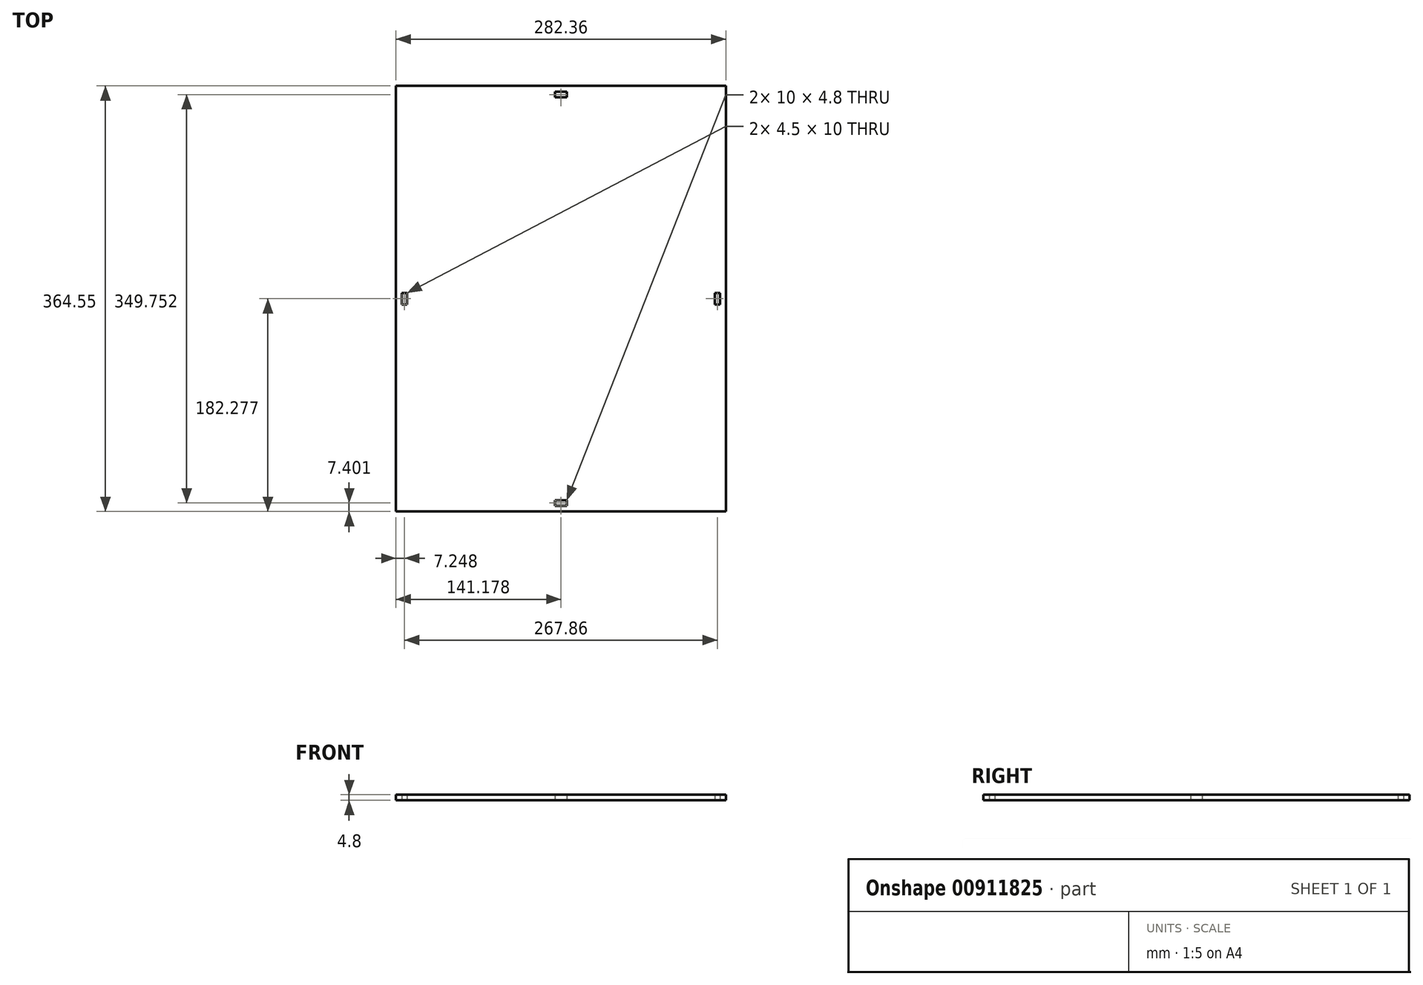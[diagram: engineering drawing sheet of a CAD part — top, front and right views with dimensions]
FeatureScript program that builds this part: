
annotation { "Feature Type Name" : "Feature", "Feature Type Description" : "" }
export const myFeature = defineFeature(function(context is Context, id is Id, definition is map)
    precondition{}
    {
        {
            var Q0;
            Q0=qCreatedBy(makeId("Top.planeOp"),FACE);
            var sketch = newSketch(context, id + "F0", { "sketchPlane" : qUnion([Q0])});
            skLineSegment(sketch, "E0.bottom", {"start": v(-131.6, 255.96) * mm, "end": v(-0.42, 255.96) * mm});
            skLineSegment(sketch, "E0.top", {"start": v(-131.6, -98.59) * mm, "end": v(-0.42, -98.59) * mm});
            skLineSegment(sketch, "E0.left", {"start": v(-131.6, 255.96) * mm, "end": v(-131.6, 83.69) * mm});
            skLineSegment(sketch, "E0.right", {"start": v(140.76, 255.96) * mm, "end": v(140.76, 83.69) * mm});
            skLineSegment(sketch, "E1", {"start": v(4.58, 251.16) * mm, "end": v(4.58, -93.79) * mm});
            skLineSegment(sketch, "E2", {"start": v(135.96, 78.69) * mm, "end": v(-126.8, 78.69) * mm});
            skLineSegment(sketch, "E3", {"start": v(136.26, 73.69) * mm, "end": v(140.76, 73.69) * mm});
            skLineSegment(sketch, "E4.MirrorCS", {"start": v(136.26, 83.69) * mm, "end": v(140.76, 83.69) * mm});
            skPoint(sketch, "E5.start.orphan", {"position": v(140.76, 78.69) * mm});
            skLineSegment(sketch, "E6.MirrorCS", {"start": v(-126.8, 73.69) * mm, "end": v(-131.6, 73.69) * mm});
            skLineSegment(sketch, "E7.MirrorCS", {"start": v(-126.8, 83.69) * mm, "end": v(-131.6, 83.69) * mm});
            skLineSegment(sketch, "E8", {"start": v(4.58, 251.16) * mm, "end": v(9.58, 251.16) * mm});
            skLineSegment(sketch, "E9", {"start": v(9.58, 251.16) * mm, "end": v(9.58, 255.96) * mm});
            skLineSegment(sketch, "E10.MirrorCS", {"start": v(4.58, 251.16) * mm, "end": v(-0.42, 251.16) * mm});
            skLineSegment(sketch, "E11.MirrorCS", {"start": v(-0.42, 251.16) * mm, "end": v(-0.42, 255.96) * mm});
            skLineSegment(sketch, "E12.MirrorCS", {"start": v(9.58, -93.79) * mm, "end": v(9.58, -98.59) * mm});
            skLineSegment(sketch, "E13.MirrorCS", {"start": v(4.58, -93.79) * mm, "end": v(9.58, -93.79) * mm});
            skLineSegment(sketch, "E14.MirrorCS", {"start": v(-0.42, -93.79) * mm, "end": v(-0.42, -98.59) * mm});
            skLineSegment(sketch, "E15.MirrorCS", {"start": v(4.58, -93.79) * mm, "end": v(-0.42, -93.79) * mm});
            skPoint(sketch, "E16.end.orphan", {"position": v(4.58, 255.96) * mm});
            skLineSegment(sketch, "E17.trimOffspring", {"start": v(9.58, 255.96) * mm, "end": v(140.76, 255.96) * mm});
            skLineSegment(sketch, "E18.trimOffspring", {"start": v(140.76, 73.69) * mm, "end": v(140.76, -98.59) * mm});
            skLineSegment(sketch, "E19.trimOffspring", {"start": v(9.58, -98.59) * mm, "end": v(140.76, -98.59) * mm});
            skPoint(sketch, "E20.orphan", {"position": v(4.58, -98.59) * mm});
            skPoint(sketch, "E21.orphan", {"position": v(-131.6, 78.69) * mm});
            skLineSegment(sketch, "E22.trimOffspring", {"start": v(-131.6, 73.69) * mm, "end": v(-131.6, -98.59) * mm});
            skLineSegment(sketch, "E23", {"start": v(140.76, 83.69) * mm, "end": v(140.76, 73.69) * mm});
            skLineSegment(sketch, "E24", {"start": v(9.58, 255.96) * mm, "end": v(-0.42, 255.96) * mm});
            skLineSegment(sketch, "E25", {"start": v(9.58, -98.59) * mm, "end": v(-0.42, -98.59) * mm});
            skLineSegment(sketch, "E26", {"start": v(-131.6, 83.69) * mm, "end": v(-131.6, 73.69) * mm});
            skLineSegment(sketch, "E27.6", {"start": v(140.76, 260.96) * mm, "end": v(140.76, 83.69) * mm});
            skLineSegment(sketch, "E28", {"start": v(140.76, 78.69) * mm, "end": v(136.26, 78.69) * mm});
            skLineSegment(sketch, "E29", {"start": v(136.26, 78.69) * mm, "end": v(136.26, 83.69) * mm});
            skLineSegment(sketch, "E30", {"start": v(136.26, 83.69) * mm, "end": v(136.26, 73.69) * mm});
            skPoint(sketch, "E31.MirrorCS.end.orphan", {"position": v(135.96, 83.69) * mm});
            skPoint(sketch, "E32.start.orphan", {"position": v(135.96, 78.69) * mm});
            skPoint(sketch, "E33.orphan", {"position": v(135.96, 73.69) * mm});
            skLineSegment(sketch, "E34", {"start": v(-131.6, 78.69) * mm, "end": v(-127.1, 78.69) * mm});
            skLineSegment(sketch, "E35", {"start": v(-127.1, 83.69) * mm, "end": v(-127.1, 73.69) * mm});
            skPoint(sketch, "E36.MirrorCS.end.orphan", {"position": v(-126.8, 73.69) * mm});
            skPoint(sketch, "E37.MirrorCS.end.orphan", {"position": v(-126.8, 83.69) * mm});
            skPoint(sketch, "E37.MirrorCS.start.orphan", {"position": v(-126.8, 78.69) * mm});
            skLineSegment(sketch, "E38", {"start": v(140.76, 260.96) * mm, "end": v(145.76, 260.96) * mm});
            skLineSegment(sketch, "E39", {"start": v(-131.6, -98.59) * mm, "end": v(-131.6, -103.59) * mm});
            skLineSegment(sketch, "E40", {"start": v(-131.6, -103.59) * mm, "end": v(-136.6, -103.59) * mm});
            skLineSegment(sketch, "E41.bottom", {"start": v(-136.6, -103.59) * mm, "end": v(145.76, -103.59) * mm});
            skLineSegment(sketch, "E41.top", {"start": v(-136.6, 260.96) * mm, "end": v(145.76, 260.96) * mm});
            skLineSegment(sketch, "E41.left", {"start": v(-136.6, -103.59) * mm, "end": v(-136.6, 260.96) * mm});
            skLineSegment(sketch, "E41.right", {"start": v(145.76, -103.59) * mm, "end": v(145.76, 260.96) * mm});
            skSolve(sketch);
        }
        {
            var Q0;
            Q0=makeQuery(id+"F0.imprint","IMPRINT",FACE,{"disambiguationData":[TD([[makeQuery(id+"F0.imprint","IMPRINT",EDGE,{"derivedFrom":sQuery(id+"F0.wireOp",EDGE,"E0.right")}),-1.0]])]});
            var Q1;
            {var subQ0=sQuery(id+"F0.wireOp",EDGE,"E32");Q1=makeQuery(id+"F0.imprint","IMPRINT",FACE,{"disambiguationData":[TD([[makeQuery(id+"F0.imprint","IMPRINT",EDGE,{"derivedFrom":subQ0}),-1.0]])]});}
            var Q2;
            Q2=makeQuery(id+"F0.imprint","IMPRINT",FACE,{"disambiguationData":[TD([[makeQuery(id+"F0.imprint","IMPRINT",EDGE,{"derivedFrom":sQuery(id+"F0.wireOp",EDGE,"E0.bottom")}),-1.0]])]});
            var Q3;
            Q3=makeQuery(id+"F0.imprint","IMPRINT",FACE,{"disambiguationData":[TD([[makeQuery(id+"F0.imprint","IMPRINT",EDGE,{"derivedFrom":sQuery(id+"F0.wireOp",EDGE,"E0.bottom")}),-1.0]])]});
            var Q4;
            Q4=makeQuery(id+"F0.imprint","IMPRINT",FACE,{"disambiguationData":[TD([[makeQuery(id+"F0.imprint","IMPRINT",EDGE,{"derivedFrom":sQuery(id+"F0.wireOp",EDGE,"E0.bottom")}),1.0]])]});
            var Q5;
            Q5=makeQuery(id+"F0.imprint","IMPRINT",FACE,{"disambiguationData":[TD([[makeQuery(id+"F0.imprint","IMPRINT",EDGE,{"derivedFrom":sQuery(id+"F0.wireOp",EDGE,"E0.right")}),-1.0]])]});
            extrude(context, id + "F1", {"entities" : qUnion([Q0, Q1, Q2, Q3, Q4, Q5]), "depth" : 4.8 * mm, "offsetDistance" : 25 * mm});
        }
        {
            var Q0;
            {Q0=qUnion([makeQuery(id+"F0.imprint","IMPRINT",FACE,{"disambiguationData":[TD([[makeQuery(id+"F0.imprint","IMPRINT",EDGE,{"derivedFrom":sQuery(id+"F0.wireOp",EDGE,"E0.bottom")}),1.0]])]}),makeQuery(id+"F0.imprint","IMPRINT",FACE,{"disambiguationData":[TD([[makeQuery(id+"F0.imprint","IMPRINT",EDGE,{"derivedFrom":sQuery(id+"F0.wireOp",EDGE,"E0.top")}),-1.0]])]})]);}
            extrude(context, id + "F2", {"entities" : qUnion([Q0]), "operationType" : NewBodyOperationType.ADD, "depth" : 4.8 * mm, "offsetDistance" : 25 * mm});
        }
    });
